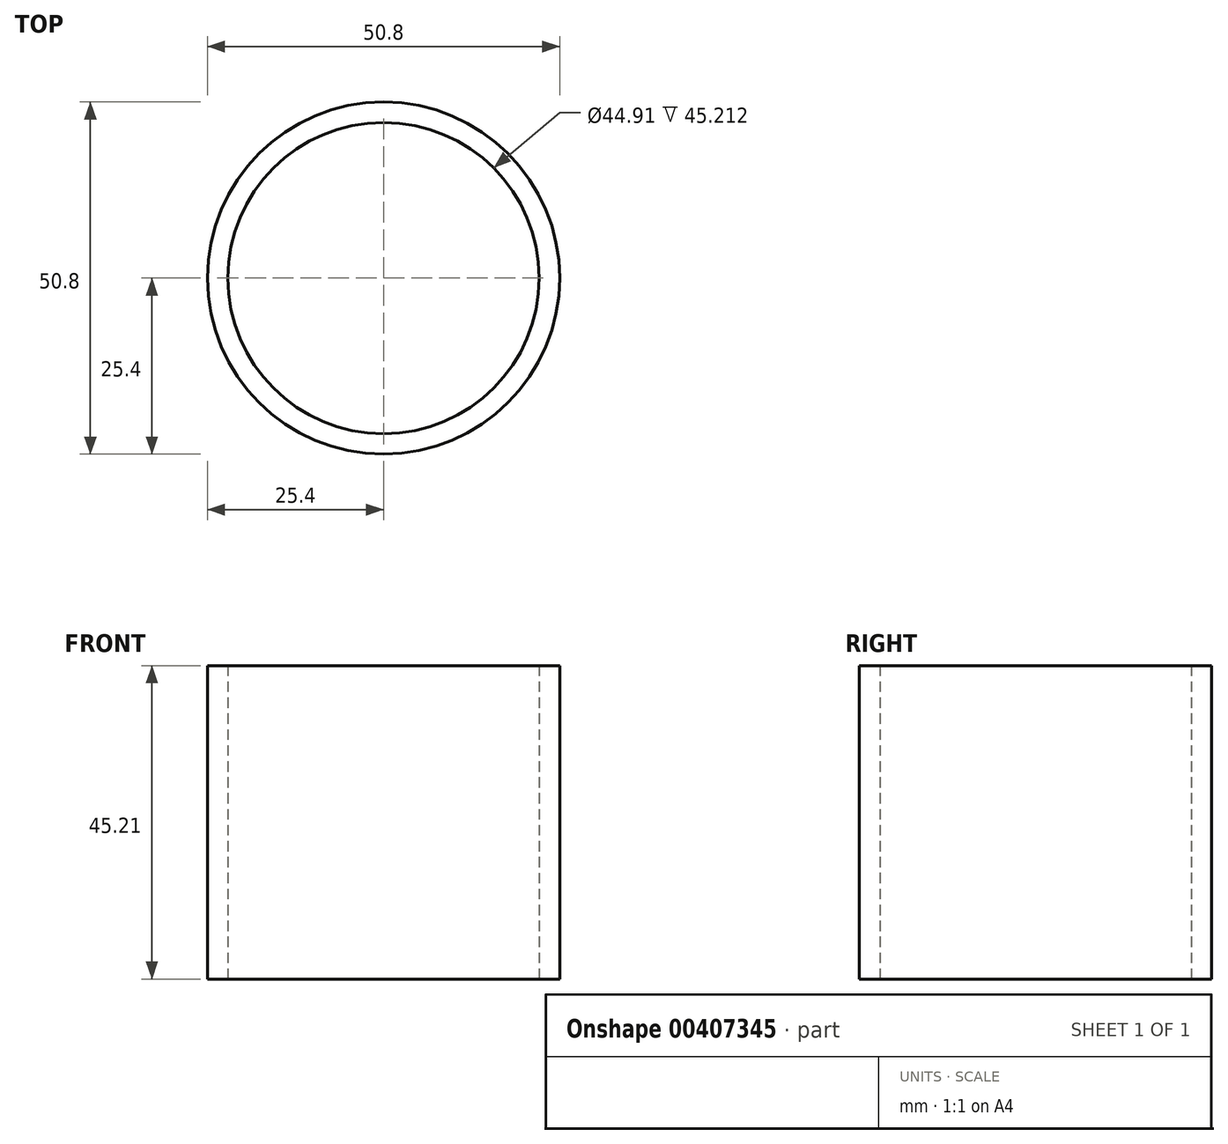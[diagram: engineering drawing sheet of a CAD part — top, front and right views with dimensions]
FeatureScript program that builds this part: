
annotation { "Feature Type Name" : "Feature", "Feature Type Description" : "" }
export const myFeature = defineFeature(function(context is Context, id is Id, definition is map)
    precondition{}
    {
        {
            var Q0;
            Q0=qCreatedBy(makeId("Top.planeOp"),FACE);
            var sketch = newSketch(context, id + "F0", { "sketchPlane" : qUnion([Q0])});
            skCircle(sketch, "E0", {"center": v(0, 0) * mm, "radius": 25.4 * mm});
            skLineSegment(sketch, "E1", {"start": v(0, 0) * mm, "end": v(25.4, 0) * mm});
            skCircle(sketch, "E2", {"center": v(0, 0) * mm, "radius": 22.45 * mm});
            skLineSegment(sketch, "E3", {"start": v(0, 0) * mm, "end": v(22.45, 0) * mm});
            skSolve(sketch);
        }
        {
            var Q0;
            Q0=makeQuery(id+"F0.imprint","IMPRINT",FACE,{"disambiguationData":[TD([[makeQuery(id+"F0.imprint","IMPRINT",EDGE,{"derivedFrom":sQuery(id+"F0.wireOp",EDGE,"E0")}),1.0]])]});
            extrude(context, id + "F1", {"entities" : qUnion([Q0]), "depth" : 45.2 * mm});
        }
    });
